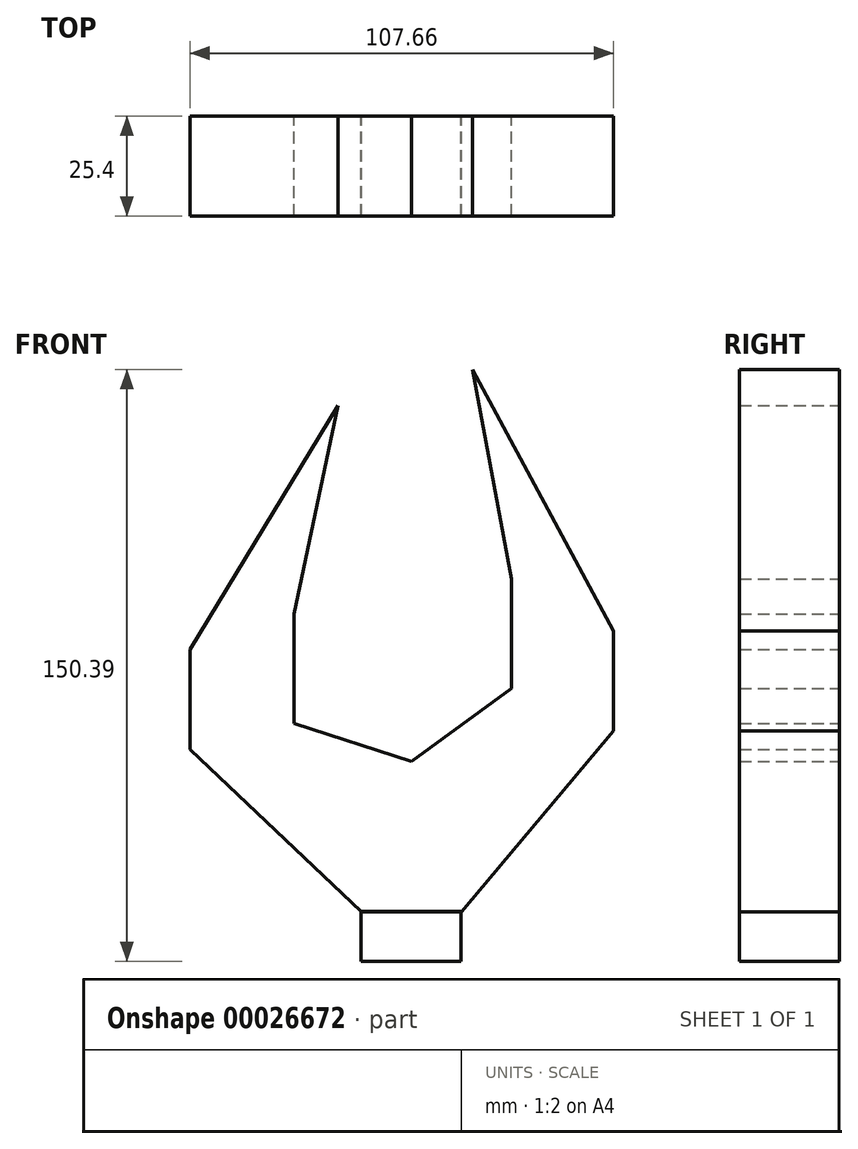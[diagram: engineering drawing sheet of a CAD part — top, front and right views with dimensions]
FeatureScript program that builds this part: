
annotation { "Feature Type Name" : "Feature", "Feature Type Description" : "" }
export const myFeature = defineFeature(function(context is Context, id is Id, definition is map)
    precondition{}
    {
        {
            var Q0;
            Q0=qCreatedBy(makeId("Front.planeOp"),FACE);
            var sketch = newSketch(context, id + "F0", { "sketchPlane" : qUnion([Q0])});
            skLineSegment(sketch, "E0", {"start": v(-28.17, -10.75) * mm, "end": v(-71.8, 30.48) * mm});
            skLineSegment(sketch, "E1", {"start": v(-71.8, 30.48) * mm, "end": v(-71.8, 55.88) * mm});
            skLineSegment(sketch, "E2", {"start": v(-71.8, 55.88) * mm, "end": v(-34.1, 117.88) * mm});
            skLineSegment(sketch, "E3", {"start": v(0, 127) * mm, "end": v(35.86, 60.6) * mm});
            skLineSegment(sketch, "E4", {"start": v(35.86, 60.6) * mm, "end": v(35.86, 35.2) * mm});
            skLineSegment(sketch, "E5", {"start": v(35.86, 35.2) * mm, "end": v(-2.77, -10.75) * mm});
            skLineSegment(sketch, "E6", {"start": v(-2.77, -10.75) * mm, "end": v(-28.17, -10.75) * mm});
            skLineSegment(sketch, "E7", {"start": v(-34.1, 117.88) * mm, "end": v(-45.33, 64.9) * mm});
            skLineSegment(sketch, "E8", {"start": v(-45.33, 64.9) * mm, "end": v(-45.33, 37.08) * mm});
            skLineSegment(sketch, "E9", {"start": v(-45.33, 37.08) * mm, "end": v(-15.47, 27.37) * mm});
            skLineSegment(sketch, "E10", {"start": v(-15.47, 27.37) * mm, "end": v(9.88, 45.92) * mm});
            skLineSegment(sketch, "E11", {"start": v(9.88, 45.92) * mm, "end": v(9.88, 73.75) * mm});
            skLineSegment(sketch, "E12", {"start": v(9.88, 73.75) * mm, "end": v(0, 127) * mm});
            skLineSegment(sketch, "E13", {"start": v(-15.47, -10.75) * mm, "end": v(-15.47, 27.37) * mm});
            skSolve(sketch);
        }
        {
            var Q0;
            Q0 = qSketchRegion(id + "F0", true);
            extrude(context, id + "F1", {"entities" : qUnion([Q0]), "depth" : 25.4 * mm});
        }
        {
            var Q0;
            Q0=qCreatedBy(makeId("Front.planeOp"),FACE);
            var sketch = newSketch(context, id + "F2", { "sketchPlane" : qUnion([Q0])});
            skLineSegment(sketch, "E14.bottom", {"start": v(-2.87, -10.7) * mm, "end": v(-28.27, -10.7) * mm});
            skLineSegment(sketch, "E14.top", {"start": v(-2.87, -23.4) * mm, "end": v(-28.27, -23.4) * mm});
            skLineSegment(sketch, "E14.left", {"start": v(-2.87, -10.7) * mm, "end": v(-2.87, -23.4) * mm});
            skLineSegment(sketch, "E14.right", {"start": v(-28.27, -10.7) * mm, "end": v(-28.27, -23.4) * mm});
            skSolve(sketch);
        }
        {
            var Q0;
            Q0=makeQuery(id+"F2.imprint","IMPRINT",FACE,{"disambiguationData":[TD([[makeQuery(id+"F2.imprint","IMPRINT",EDGE,{"derivedFrom":sQuery(id+"F2.wireOp",EDGE,"E14.bottom")}),1.0]])]});
            extrude(context, id + "F3", {"entities" : qUnion([Q0]), "depth" : 25.4 * mm});
        }
    });
